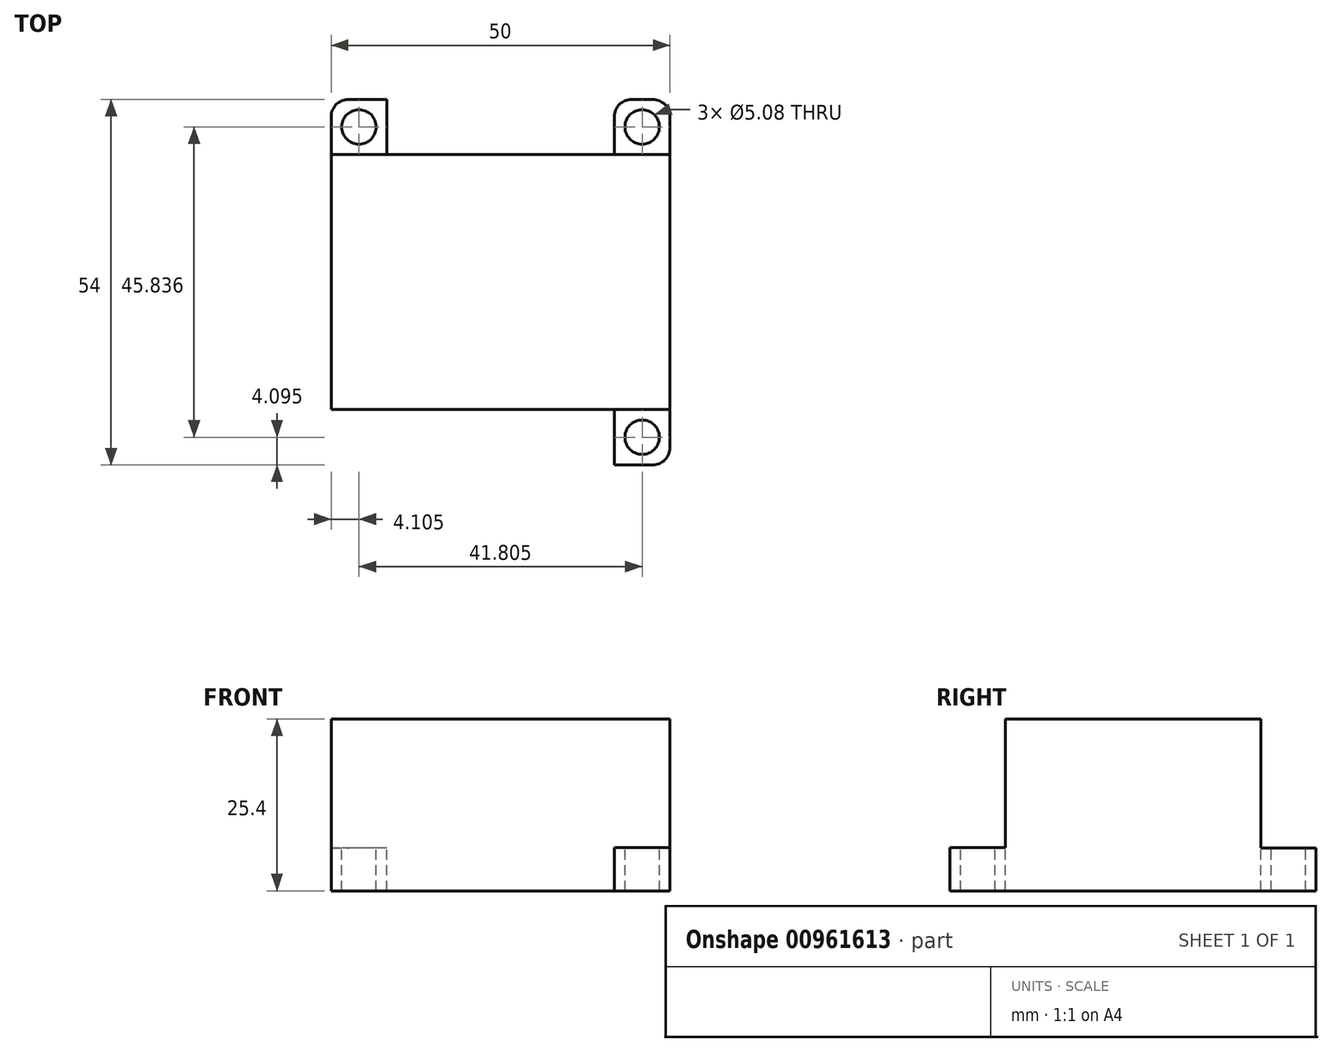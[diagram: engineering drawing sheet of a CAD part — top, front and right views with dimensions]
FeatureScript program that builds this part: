
annotation { "Feature Type Name" : "Feature", "Feature Type Description" : "" }
export const myFeature = defineFeature(function(context is Context, id is Id, definition is map)
    precondition{}
    {
        {
            var Q0;
            Q0=qCreatedBy(makeId("Top.planeOp"),FACE);
            var sketch = newSketch(context, id + "F0", { "sketchPlane" : qUnion([Q0])});
            skLineSegment(sketch, "E0.bottom", {"start": v(-50.23, 61.77) * mm, "end": v(-0.23, 61.77) * mm});
            skLineSegment(sketch, "E0.top", {"start": v(-50.23, 7.77) * mm, "end": v(-0.23, 7.77) * mm});
            skLineSegment(sketch, "E0.left", {"start": v(-50.23, 61.77) * mm, "end": v(-50.23, 7.77) * mm});
            skLineSegment(sketch, "E0.right", {"start": v(-0.23, 61.77) * mm, "end": v(-0.23, 7.77) * mm});
            skSolve(sketch);
        }
        {
            var Q0;
            Q0 = qSketchRegion(id + "F0", true);
            extrude(context, id + "F1", {"entities" : qUnion([Q0]), "depth" : 25.4 * mm, "offsetDistance" : 25.4 * mm});
        }
        {
            var Q0;
            Q0=makeQuery(id+"F1.opExtrude","CAP_FACE",FACE,{"disambiguationData":[OSD([sQuery(id+"F0.wireOp",EDGE,"E0.bottom"),sQuery(id+"F0.wireOp",EDGE,"E0.top"),sQuery(id+"F0.wireOp",EDGE,"E0.left"),sQuery(id+"F0.wireOp",EDGE,"E0.right")])],"isStart":false});
            var sketch = newSketch(context, id + "F2", { "sketchPlane" : qUnion([Q0])});
            skLineSegment(sketch, "E1.bottom", {"start": v(-50.23, 7.77) * mm, "end": v(-8.41, 7.77) * mm});
            skLineSegment(sketch, "E1.top", {"start": v(-50.23, 15.97) * mm, "end": v(-8.41, 15.97) * mm});
            skLineSegment(sketch, "E1.left", {"start": v(-50.23, 7.77) * mm, "end": v(-50.23, 15.97) * mm});
            skLineSegment(sketch, "E1.right", {"start": v(-8.41, 7.77) * mm, "end": v(-8.41, 15.97) * mm});
            skSolve(sketch);
        }
        {
            var Q0;
            Q0 = qSketchRegion(id + "F2", true);
            extrude(context, id + "F3", {"entities" : qUnion([Q0]), "operationType" : NewBodyOperationType.REMOVE, "oppositeDirection" : true, "depth" : 50.8 * mm, "offsetDistance" : 25.4 * mm});
        }
        {
            var Q0;
            Q0=makeQuery(id+"F3.boolean.opBoolean","COPY",FACE,{"derivedFrom":makeQuery(id+"F3.opExtrude","SWEPT_FACE",FACE,{"disambiguationData":[OSD([sQuery(id+"F2.wireOp",EDGE,"E1.right")])]})});
            var sketch = newSketch(context, id + "F4", { "sketchPlane" : qUnion([Q0])});
            skLineSegment(sketch, "E2.bottom", {"start": v(-15.97, 25.4) * mm, "end": v(-7.77, 25.4) * mm});
            skLineSegment(sketch, "E2.top", {"start": v(-15.97, 6.38) * mm, "end": v(-7.77, 6.38) * mm});
            skLineSegment(sketch, "E2.left", {"start": v(-15.97, 25.4) * mm, "end": v(-15.97, 6.38) * mm});
            skLineSegment(sketch, "E2.right", {"start": v(-7.77, 25.4) * mm, "end": v(-7.77, 6.38) * mm});
            skSolve(sketch);
        }
        {
            var Q0;
            Q0 = qSketchRegion(id + "F4", true);
            extrude(context, id + "F5", {"entities" : qUnion([Q0]), "operationType" : NewBodyOperationType.REMOVE, "oppositeDirection" : true, "depth" : 25.4 * mm, "offsetDistance" : 25.4 * mm});
        }
        {
            var Q0;
            Q0=makeQuery(id+"F5.boolean.opBoolean","COPY",FACE,{"derivedFrom":makeQuery(id+"F5.opExtrude","SWEPT_FACE",FACE,{"disambiguationData":[OSD([sQuery(id+"F4.wireOp",EDGE,"E2.top")])]})});
            var sketch = newSketch(context, id + "F6", { "sketchPlane" : qUnion([Q0])});
            skPoint(sketch, "E3", {"position": v(-4.32, 11.87) * mm});
            skPoint(sketch, "E3.positionSnap0", {"position": v(-0.23, 11.87) * mm});
            skPoint(sketch, "E3.positionSnap1", {"position": v(-4.32, 7.77) * mm});
            skSolve(sketch);
        }
        {
            var Q0;
            Q0=sQuery(id+"F6.wireOp",VERTEX,"E3");
            var Q1;
            Q1=makeQuery(id+"F1.opExtrude","SWEPT_BODY",BODY,{"disambiguationData":[OSD([sQuery(id+"F0.wireOp",EDGE,"E0.bottom"),sQuery(id+"F0.wireOp",EDGE,"E0.top"),sQuery(id+"F0.wireOp",EDGE,"E0.left"),sQuery(id+"F0.wireOp",EDGE,"E0.right")])]});
            hole(context, id + "F7", {"style" : HoleStyle.SIMPLE, "endStyle" : HoleEndStyle.THROUGH, "holeDiameter" : 5.08 * mm, "majorDiameter" : 6.35 * mm, "isTappedThrough" : true, "tappedDepth" : 12.7 * mm, "tapClearance" : 3, "locations" : qUnion([Q0]), "scope" : qUnion([Q1])});
        }
        {
            var Q0;
            Q0=makeQuery(id+"F3.boolean.opBoolean","COPY",EDGE,{"derivedFrom":makeQuery(id+"F3.opExtrude","SWEPT_EDGE",EDGE,{"disambiguationData":[OSD([sQuery(id+"F0.wireOp",EDGE,"E0.top"),sQuery(id+"F2.wireOp",EDGE,"E1.bottom"),sQuery(id+"F2.wireOp",EDGE,"E1.right")])]})});
            var Q1;
            Q1=makeQuery(id+"F1.opExtrude","SWEPT_EDGE",EDGE,{"disambiguationData":[OSD([sQuery(id+"F0.wireOp",EDGE,"E0.top"),sQuery(id+"F0.wireOp",EDGE,"E0.right")])]});
            fillet(context, id + "F8", {"entities" : qUnion([Q0, Q1]), "radius" : 2.54 * mm, "tangentPropagation" : true, "allowEdgeOverflow" : false});
        }
        {
            var Q0;
            Q0=makeQuery(id+"F1.opExtrude","SWEPT_FACE",FACE,{"disambiguationData":[OSD([sQuery(id+"F0.wireOp",EDGE,"E0.bottom")])]});
            var sketch = newSketch(context, id + "F9", { "sketchPlane" : qUnion([Q0])});
            skLineSegment(sketch, "E4.bottom", {"start": v(0.23, 25.4) * mm, "end": v(50.23, 25.4) * mm});
            skLineSegment(sketch, "E4.top", {"start": v(0.23, 6.35) * mm, "end": v(50.23, 6.35) * mm});
            skLineSegment(sketch, "E4.left", {"start": v(0.23, 25.4) * mm, "end": v(0.23, 6.35) * mm});
            skLineSegment(sketch, "E4.right", {"start": v(50.23, 25.4) * mm, "end": v(50.23, 6.35) * mm});
            skSolve(sketch);
        }
        {
            var Q0;
            Q0 = qSketchRegion(id + "F9", true);
            extrude(context, id + "F10", {"entities" : qUnion([Q0]), "operationType" : NewBodyOperationType.REMOVE, "oppositeDirection" : true, "depth" : 8.13 * mm, "offsetDistance" : 25.4 * mm});
        }
        {
            var Q0;
            Q0=makeQuery(id+"F10.boolean.opBoolean","COPY",FACE,{"derivedFrom":makeQuery(id+"F10.opExtrude","SWEPT_FACE",FACE,{"disambiguationData":[OSD([sQuery(id+"F9.wireOp",EDGE,"E4.top")])]})});
            var sketch = newSketch(context, id + "F11", { "sketchPlane" : qUnion([Q0])});
            skLineSegment(sketch, "E5.bottom", {"start": v(-42.02, 61.77) * mm, "end": v(-8.43, 61.77) * mm});
            skLineSegment(sketch, "E5.top", {"start": v(-42.02, 53.64) * mm, "end": v(-8.43, 53.64) * mm});
            skLineSegment(sketch, "E5.left", {"start": v(-42.02, 61.77) * mm, "end": v(-42.02, 53.64) * mm});
            skLineSegment(sketch, "E5.right", {"start": v(-8.43, 61.77) * mm, "end": v(-8.43, 53.64) * mm});
            skSolve(sketch);
        }
        {
            var Q0;
            Q0 = qSketchRegion(id + "F11", true);
            extrude(context, id + "F12", {"entities" : qUnion([Q0]), "operationType" : NewBodyOperationType.REMOVE, "oppositeDirection" : true, "depth" : 25.4 * mm, "offsetDistance" : 25.4 * mm});
        }
        {
            var Q0;
            {var subQ0=sQuery(id+"F9.wireOp",EDGE,"E4.top");Q0=makeQuery(id+"F12.boolean.opBoolean","SPLIT",FACE,{"disambiguationData":[TD([makeQuery(id+"F1.opExtrude","SWEPT_FACE",FACE,{"disambiguationData":[OSD([sQuery(id+"F0.wireOp",EDGE,"E0.left")])]})])],"derivedFrom":makeQuery(id+"F10.boolean.opBoolean","COPY",FACE,{"derivedFrom":makeQuery(id+"F10.opExtrude","SWEPT_FACE",FACE,{"disambiguationData":[OSD([subQ0])]})})});}
            var sketch = newSketch(context, id + "F13", { "sketchPlane" : qUnion([Q0])});
            skPoint(sketch, "E6", {"position": v(-46.13, 57.7) * mm});
            skPoint(sketch, "E6.positionSnap0", {"position": v(-46.13, 61.77) * mm});
            skPoint(sketch, "E6.positionSnap1", {"position": v(-50.23, 57.7) * mm});
            skSolve(sketch);
        }
        {
            var Q0;
            {var subQ0=sQuery(id+"F9.wireOp",EDGE,"E4.top");Q0=makeQuery(id+"F12.boolean.opBoolean","SPLIT",FACE,{"disambiguationData":[TD([makeQuery(id+"F1.opExtrude","SWEPT_FACE",FACE,{"disambiguationData":[OSD([sQuery(id+"F0.wireOp",EDGE,"E0.right")])]})])],"derivedFrom":makeQuery(id+"F10.boolean.opBoolean","COPY",FACE,{"derivedFrom":makeQuery(id+"F10.opExtrude","SWEPT_FACE",FACE,{"disambiguationData":[OSD([subQ0])]})})});}
            var sketch = newSketch(context, id + "F14", { "sketchPlane" : qUnion([Q0])});
            skPoint(sketch, "E7", {"position": v(-4.33, 57.7) * mm});
            skPoint(sketch, "E7.positionSnap0", {"position": v(-0.23, 57.7) * mm});
            skPoint(sketch, "E7.positionSnap1", {"position": v(-4.33, 61.77) * mm});
            skSolve(sketch);
        }
        {
            var Q0;
            Q0=sQuery(id+"F14.wireOp",VERTEX,"E7");
            var Q1;
            Q1=sQuery(id+"F13.wireOp",VERTEX,"E6");
            var Q2;
            Q2=makeQuery(id+"F1.opExtrude","SWEPT_BODY",BODY,{"disambiguationData":[OSD([sQuery(id+"F0.wireOp",EDGE,"E0.bottom"),sQuery(id+"F0.wireOp",EDGE,"E0.top"),sQuery(id+"F0.wireOp",EDGE,"E0.left"),sQuery(id+"F0.wireOp",EDGE,"E0.right")])]});
            hole(context, id + "F15", {"style" : HoleStyle.SIMPLE, "endStyle" : HoleEndStyle.THROUGH, "holeDiameter" : 5.08 * mm, "majorDiameter" : 6.35 * mm, "isTappedThrough" : true, "tappedDepth" : 12.7 * mm, "tapClearance" : 3, "locations" : qUnion([Q0, Q1]), "scope" : qUnion([Q2])});
        }
        {
            var Q0;
            Q0=makeQuery(id+"F1.opExtrude","SWEPT_EDGE",EDGE,{"disambiguationData":[OSD([sQuery(id+"F0.wireOp",EDGE,"E0.bottom"),sQuery(id+"F0.wireOp",EDGE,"E0.left")])]});
            var Q1;
            Q1=makeQuery(id+"F12.boolean.opBoolean","COPY",EDGE,{"derivedFrom":makeQuery(id+"F12.opExtrude","SWEPT_EDGE",EDGE,{"disambiguationData":[OSD([sQuery(id+"F9.wireOp",EDGE,"E4.top"),sQuery(id+"F11.wireOp",EDGE,"E5.bottom"),sQuery(id+"F11.wireOp",EDGE,"E5.left")])]})});
            var Q2;
            Q2=makeQuery(id+"F12.boolean.opBoolean","COPY",EDGE,{"derivedFrom":makeQuery(id+"F12.opExtrude","SWEPT_EDGE",EDGE,{"disambiguationData":[OSD([sQuery(id+"F9.wireOp",EDGE,"E4.top"),sQuery(id+"F11.wireOp",EDGE,"E5.bottom"),sQuery(id+"F11.wireOp",EDGE,"E5.right")])]})});
            var Q3;
            Q3=makeQuery(id+"F1.opExtrude","SWEPT_EDGE",EDGE,{"disambiguationData":[OSD([sQuery(id+"F0.wireOp",EDGE,"E0.bottom"),sQuery(id+"F0.wireOp",EDGE,"E0.right")])]});
            fillet(context, id + "F16", {"entities" : qUnion([Q0, Q1, Q2, Q3]), "radius" : 2.54 * mm, "tangentPropagation" : true, "allowEdgeOverflow" : false});
        }
    });
